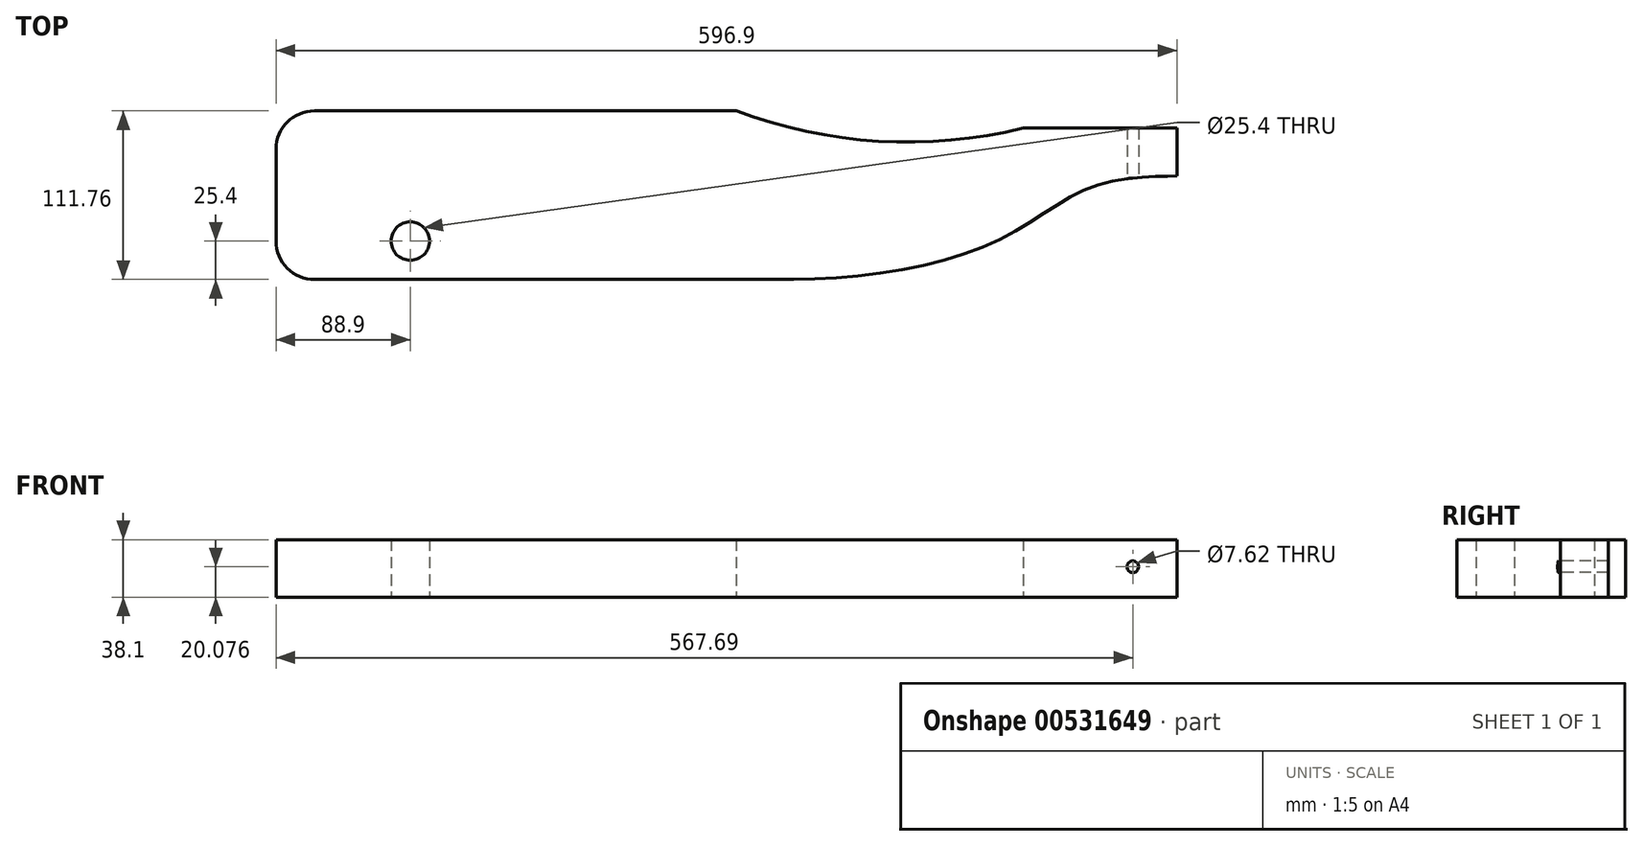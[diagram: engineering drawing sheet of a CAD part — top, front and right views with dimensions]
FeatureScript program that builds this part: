
annotation { "Feature Type Name" : "Feature", "Feature Type Description" : "" }
export const myFeature = defineFeature(function(context is Context, id is Id, definition is map)
    precondition{}
    {
        {
            var Q0;
            Q0=qCreatedBy(makeId("Top.planeOp"),FACE);
            var sketch = newSketch(context, id + "F0", { "sketchPlane" : qUnion([Q0])});
            skLineSegment(sketch, "E0", {"start": v(-298.45, 0) * mm, "end": v(298.45, 0) * mm, "construction": true});
            skLineSegment(sketch, "E1", {"start": v(0, 55.88) * mm, "end": v(0, -55.88) * mm, "construction": true});
            skLineSegment(sketch, "E2.bottom", {"start": v(-298.45, -55.88) * mm, "end": v(298.45, -55.88) * mm});
            skLineSegment(sketch, "E2.left", {"start": v(-298.45, -55.88) * mm, "end": v(-298.45, 55.88) * mm});
            skPoint(sketch, "E2.middle", {"position": v(0, 0) * mm});
            skPoint(sketch, "E3", {"position": v(298.45, 44.45) * mm});
            skLineSegment(sketch, "E4", {"start": v(298.45, 44.45) * mm, "end": v(196.65, 44.45) * mm});
            skArc(sketch, "E5", {"start": v(6.35, 55.88) * mm, "mid": v(100.64, 35.8) * mm, "end": v(196.65, 44.45) * mm});
            skPoint(sketch, "E6", {"position": v(100.64, 35.8) * mm});
            skLineSegment(sketch, "E7", {"start": v(-298.45, 55.88) * mm, "end": v(6.35, 55.88) * mm});
            skLineSegment(sketch, "E8", {"start": v(6.35, 55.88) * mm, "end": v(298.45, 55.88) * mm, "construction": true});
            skLineSegment(sketch, "E9", {"start": v(298.45, 44.45) * mm, "end": v(298.45, 12.7) * mm});
            skLineSegment(sketch, "E10", {"start": v(298.45, 12.7) * mm, "end": v(298.45, -55.88) * mm, "construction": true});
            skLineSegment(sketch, "E11", {"start": v(298.45, 44.45) * mm, "end": v(298.45, 55.88) * mm, "construction": true});
            skFitSpline(sketch, "E12", {"points": [v(298.45, 12.7) * mm, v(245.66, 6.7) * mm, v(176.56, -31.47) * mm, v(44.45, -55.88) * mm], "startDerivative": vector(-126.56, -5.23) * mm, "endDerivative": vector(-314.3, 0) * mm});
            skArc(sketch, "E13", {"start": v(-298.45, -30.48) * mm, "mid": v(-291.01, -48.44) * mm, "end": v(-273.05, -55.88) * mm});
            skArc(sketch, "E14", {"start": v(-273.05, 55.88) * mm, "mid": v(-291.01, 48.44) * mm, "end": v(-298.45, 30.48) * mm});
            skCircle(sketch, "E15", {"center": v(-209.55, -30.48) * mm, "radius": 12.7 * mm});
            skLineSegment(sketch, "E16", {"start": v(-209.55, -30.48) * mm, "end": v(-298.45, -30.48) * mm, "construction": true});
            skLineSegment(sketch, "E17", {"start": v(-209.55, -30.48) * mm, "end": v(-209.55, -55.88) * mm, "construction": true});
            skSolve(sketch);
        }
        {
            var Q0;
            Q0=makeQuery(id+"F0.imprint","IMPRINT",FACE,{"disambiguationData":[TD([[makeQuery(id+"F0.imprint","IMPRINT",EDGE,{"derivedFrom":sQuery(id+"F0.wireOp",EDGE,"E4")}),1.0]])]});
            extrude(context, id + "F1", {"entities" : qUnion([Q0]), "depth" : 38.1 * mm, "offsetDistance" : 25.4 * mm});
        }
        {
            var Q0;
            Q0=makeQuery(id+"F0.imprint","IMPRINT",FACE,{"disambiguationData":[TD([[makeQuery(id+"F0.imprint","IMPRINT",EDGE,{"derivedFrom":sQuery(id+"F0.wireOp",EDGE,"E15")}),1.0]])]});
            var Q1;
            Q1=sQuery(id+"F0.wireOp",EDGE,"E15");
            extrude(context, id + "F2", {"entities" : qUnion([Q0]), "operationType" : NewBodyOperationType.REMOVE, "surfaceEntities" : qUnion([Q1]), "depth" : 38.1 * mm, "offsetDistance" : 25.4 * mm});
        }
        {
            var Q0;
            Q0=qCreatedBy(makeId("Front.planeOp"),FACE);
            var sketch = newSketch(context, id + "F3", { "sketchPlane" : qUnion([Q0])});
            skLineSegment(sketch, "E18", {"start": v(298.45, 20.08) * mm, "end": v(269.24, 20.08) * mm, "construction": true});
            skCircle(sketch, "E19", {"center": v(269.24, 20.08) * mm, "radius": 3.81 * mm});
            skSolve(sketch);
        }
        {
            var Q0;
            Q0=makeQuery(id+"F3.imprint","IMPRINT",FACE,{"disambiguationData":[TD([[makeQuery(id+"F3.imprint","IMPRINT",EDGE,{"derivedFrom":sQuery(id+"F3.wireOp",EDGE,"E19")}),1.0]])]});
            var Q1;
            Q1=sQuery(id+"F3.wireOp",EDGE,"E19");
            extrude(context, id + "F4", {"entities" : qUnion([Q0]), "operationType" : NewBodyOperationType.REMOVE, "surfaceEntities" : qUnion([Q1]), "oppositeDirection" : true, "depth" : 44.45 * mm, "offsetDistance" : 25.4 * mm});
        }
    });
